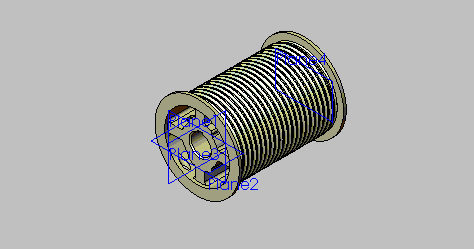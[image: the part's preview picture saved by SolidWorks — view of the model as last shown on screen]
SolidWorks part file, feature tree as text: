
SOLIDWORKS PART (.sldprt)
format: sldprt  version: not decoded by parser v0  size: 11,364,352 bytes
history: native  units: mm
features: sketch x16, plane x7, cut_extrude x7, extrude x3, cut_revolve x2, material x1, revolve x1, pattern_linear x1, chamfer x1, hole x1, mirror x1 (+10 scaffold rows collapsed)
feature tree (51):
  scaffold x10  (default folders/planes/origin — collapsed)
  material  "Material <not specified>"
  plane  "Plane1"  Offset=0mm
  plane  "Plane2"  Offset=0mm
  plane  "Plane3"  Offset=0mm
  plane  "Plane4"  Offset=304.8mm
  sketch  "Sketch1"  dims[D1=201.6125mm]
  extrude  "Extrude1"  [1 undecoded]
  sketch  "Sketch2"  dims[D1=239.7125mm D2=201.6125mm]
  extrude  "Extrude2"  Depth=7.9375mm
  sketch  "Sketch3"  dims[D1=239.7125mm D2=201.6125mm]
  extrude  "Extrude3"  Depth=7.9375mm
  sketch  "Sketch4"  dims[D1=54.0131mm]
  cut_extrude  "Cut-Extrude1"  [1 undecoded]
  sketch  "Sketch5"  dims[D1=~28.53055mm]
  cut_extrude  "Cut-Extrude2"  Depth=88.9mm
  sketch  "Sketch6"  dims[D1=184.15mm]
  cut_extrude  "Cut-Extrude3"  Depth=8.73125mm
  sketch  "Sketch7"  dims[D1=184.15mm]
  cut_extrude  "Cut-Extrude4"  Depth=8.73125mm
  sketch  "Sketch8"  dims[D1=5.9436mm D2=5.9436mm D3=1.143mm D4=7.9375mm D5=~100.80625mm]
  revolve  "Revolve1"  Angle=360deg
  pattern_linear  "LPattern1"  Count1=23 Count2=1 Spacing1=12.7mm Spacing2=50mm
  sketch  "Sketch9"  dims[c1.D1=5.9436mm c1.D2=5.9436mm c1.D14=5.9436mm c1.D15=5.9436mm c2.D14=5.9436mm c2.D15=5.9436mm c2.D2=~23.167249mm c2.D3=~3.939521mm c2.D4=~14.36684mm c2.D5=7.9375mm c2.D6=~104.745771mm c2.D7=3.175mm c3.D6=~106.748784mm c3.D7=~106.748784mm c4.D6=3.175mm c4.D7=~13.53342mm c4.D8=~3.400087mm c4.D9=~104.745771mm c4.D10=7.9375mm c4.D11=3.175mm c4.D12=~14.36684mm c4.D13=~3.939521mm c4.D16=~104.483829mm c4.D17=~2.949913mm c4.D18=~5.708463mm c5.D13=~3.939521mm c5.D18=~3.939521mm c6.D13=~3.939521mm c6.D18=~13.53342mm c6.D10=~13.53342mm c7.D18=7.9375mm c7.D10=~14.36684mm c7.D11=7.9375mm c7.D12=3.175mm c7.D13=~3.939521mm c7.D15=~21.164235mm c7.D16=~3.400087mm c7.D17=~13.53342mm c8.D18=104.7496mm]
  cut_revolve  "Cut-Revolve1"  Angle=360deg
  plane  "Plane6"
  sketch  "Sketch10"  dims[D1=15.875mm D2=17.4625mm D3=82.55mm]
  cut_extrude  "Cut-Extrude5"  [1 undecoded]
  chamfer  "Chamfer1"  Distance=3.175mm Angle=45deg
  plane  "Plane7"
  plane  "Plane9"  Offset=100.80625mm
  sketch  "Sketch39"
  hole  "1/2-13 Tapped Hole6"  Diameter=10.71626mm Depth=101.6mm
  sketch  "Sketch43"  dims[D1=26.9875mm]
  sketch  "Sketch42"  dims[hole-wizard template sketch: 29 standard entries collapsed; hole parameters kept: c8.Tap Drill Depth=101.6mm c8.Thread Major Dia.=12.7mm c8.Thread Depth=25.4mm c8.D5=~14.816244mm c8.Drill Angle=118.0deg]
  sketch  "Sketch44"  dims[D1=~13.49375mm]
  cut_extrude  "17/32 DRILL"  [1 undecoded]
  sketch  "Sketch45"  dims[D8=12.7mm D9=12.7mm D1=~84.92998mm D2=~84.92998mm D3=141.2875mm D4=141.2875mm D5=73.025mm D6=39.6875mm D7=39.6875mm]
  cut_revolve  "Cut-Revolve2"  Angle=360deg
  sketch  "Sketch46"  dims[c1.D1=14.2875mm c1.D2=14.2875mm c1.D4=~7.14375mm c1.D9=~7.14375mm c2.D2=66.675mm c2.D3=~46.83125mm c2.D4=7.9375mm c2.D5=14.2875mm c2.D6=66.675mm c2.D7=46.8376mm c2.D8=7.9375mm c2.D10=14.2875mm]
  cut_extrude  "Cut-Extrude7"  [1 undecoded]
  mirror  "Mirror1"
decode coverage: 26 of 33 modeling features carry decoded parameters
note: ~ marks probable driven/reference dimensions
note: 5 parameter values undecoded
summary: no parameter record found for 5 features
note: suppression state not decoded; provenance and decode notes live in map.json
